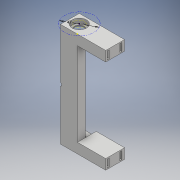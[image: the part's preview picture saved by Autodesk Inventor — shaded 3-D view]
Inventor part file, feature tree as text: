
AUTODESK INVENTOR PART (.ipt)
format: ipt  version: 2018 (Build 220112000, 112)  size: 595,968 bytes
history: native  units: mm
features: sketch x19, extrude x17, fillet x4
ambient origin geometry x8: Origin, YZ Plane, XZ Plane, XY Plane, X Axis, Y Axis, Z Axis, Center Point
bodies: Solid1 (feature_tree)
feature tree (40):
  extrude  "Extrusion1"  Depth=165.0mm
  extrude  "Extrusion2"  Depth=8.5mm
  extrude  "Extrusion3"  Depth=25.0mm TaperAngle=0.0deg
  extrude  "Extrusion4"  Depth=22.75mm
  extrude  "Extrusion5"  Depth=7.1mm
  extrude  "Extrusion6"  Depth=7.1mm TaperAngle=0.0deg
  fillet  "Fillet1"  Radius=5.0mm
  extrude  "Extrusion7"  Depth=10.0mm TaperAngle=0.0deg
  fillet  "Fillet2"  Radius=2.0mm
  extrude  "Extrusion8"  Depth=8.0mm
  extrude  "Extrusion9"  Depth=16.0mm
  fillet  "Fillet3"  Radius=8.0mm
  extrude  "Extrusion10"  Depth=6.0mm
  extrude  "Extrusion11"  Depth=3.5mm
  fillet  "Fillet4"  Radius=12.25mm
  sketch  "Sketch12"  dims[d33=3.5mm d34=12.25mm]
  extrude  "Extrusion12"  Depth=12.25mm
  extrude  "Extrusion13"  Depth=3.5mm
  extrude  "Extrusion14"  Depth=40.0mm
  sketch  "Sketch16"  dims[d42=1.0mm d43=2.0mm]
  extrude  "Extrusion15"  Depth=8.0mm
  extrude  "Extrusion16"  Depth=2.0mm
  extrude  "Extrusion17"  Depth=6.0mm
  sketch  "Sketch1"  dims[d0=25.0mm d1=165.0mm]
  sketch  "Sketch2"  dims[d2=3.0mm d3=0.0mm d4=8.5mm]
  sketch  "Sketch3"  dims[d5=8.5mm d6=25.0mm d7=0.0mm]
  sketch  "Sketch4"  dims[d8=25.0mm d9=22.75mm]
  sketch  "Sketch5"  dims[d10=7.1mm d11=0.0mm d12=15.5mm]
  sketch  "Sketch6"  dims[d13=165.0mm d14=0.0mm d15=7.1mm d16=0.0mm d17=5.0mm]
  sketch  "Sketch7"  dims[d18=5.0mm d19=10.0mm d20=0.0mm d21=2.0mm]
  sketch  "Sketch8"  dims[d22=16.0mm d23=8.0mm]
  sketch  "Sketch9"  dims[d24=16.0mm d25=16.0mm d26=8.0mm]
  sketch  "Sketch10"  dims[d27=45.0mm d28=0.0mm d29=6.0mm]
  sketch  "Sketch11"  dims[d30=12.25mm d31=3.5mm d32=12.25mm]
  sketch  "Sketch13"  dims[d35=12.25mm d36=3.5mm]
  sketch  "Sketch14"  dims[d37=40.0mm d38=0.0mm d39=1.0mm]
  sketch  "Sketch15"  dims[d40=2.0mm d41=8.0mm]
  sketch  "Sketch17"  dims[d44=12.0mm d45=0.0mm d46=6.0mm]
  sketch  "Sketch18"  dims[d47=6.0mm]
  sketch  "Sketch19"  dims[d48=4.0mm d49=8.0mm d50=6.5mm d51=0.0mm d52=6.35mm d53=8.0mm d54=0.0mm d55=6.5mm d56=47.0mm d57=1.0mm d58=7.0mm d59=0.0mm d60=7.1mm d61=0.0mm d62=14.5mm d63=0.0mm d64=2.0mm d65=0.0mm d66=8.5mm d67=2.0mm d68=0.0mm d69=20.0mm d70=0.0mm]
